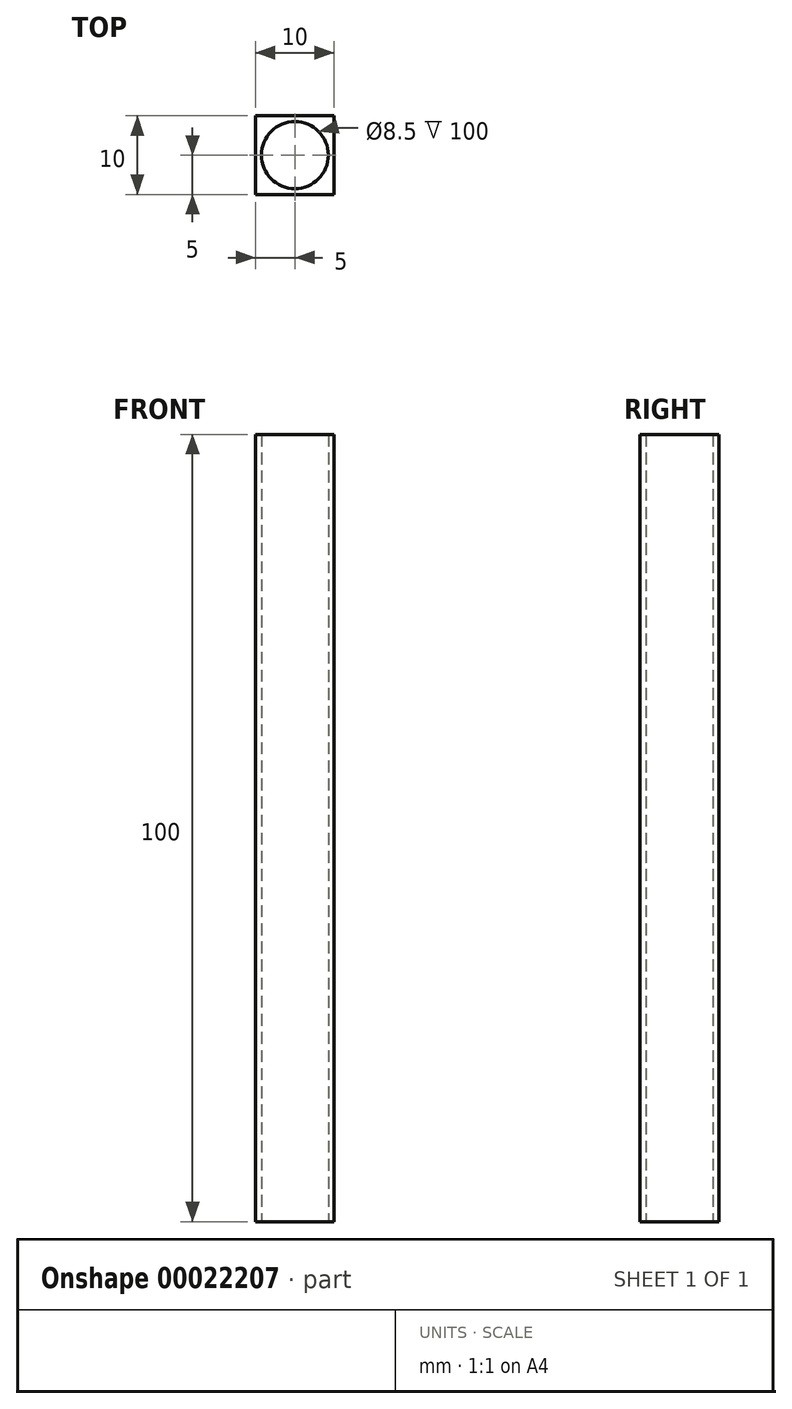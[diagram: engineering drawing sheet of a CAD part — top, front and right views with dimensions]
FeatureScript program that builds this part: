
annotation { "Feature Type Name" : "Feature", "Feature Type Description" : "" }
export const myFeature = defineFeature(function(context is Context, id is Id, definition is map)
    precondition{}
    {
        {
            var Q0;
            Q0=qCreatedBy(makeId("Top.planeOp"),FACE);
            var sketch = newSketch(context, id + "F0", { "sketchPlane" : qUnion([Q0])});
            skLineSegment(sketch, "E0.rect.bottom", {"start": v(4.5, 5) * mm, "end": v(-4.5, 5) * mm});
            skLineSegment(sketch, "E0.rect.top", {"start": v(4.5, -5) * mm, "end": v(-4.5, -5) * mm});
            skLineSegment(sketch, "E0.rect.left", {"start": v(5, 4.5) * mm, "end": v(5, -4.5) * mm});
            skLineSegment(sketch, "E0.rect.right", {"start": v(-5, 4.5) * mm, "end": v(-5, -4.5) * mm});
            skPoint(sketch, "E0.rect.middle", {"position": v(0, 0) * mm});
            skCircle(sketch, "E1", {"center": v(0, 0) * mm, "radius": 4.25 * mm});
            skPoint(sketch, "E2.visualSharp", {"position": v(-5, 5) * mm});
            skPoint(sketch, "E3.visualSharp", {"position": v(5, 5) * mm});
            skPoint(sketch, "E4.visualSharp", {"position": v(5, -5) * mm});
            skPoint(sketch, "E5.visualSharp", {"position": v(-5, -5) * mm});
            skLineSegment(sketch, "E6", {"start": v(-4.5, 5) * mm, "end": v(-5, 5) * mm});
            skLineSegment(sketch, "E7", {"start": v(-5, 4.5) * mm, "end": v(-5, 5) * mm});
            skLineSegment(sketch, "E8", {"start": v(4.5, 5) * mm, "end": v(5, 5) * mm});
            skLineSegment(sketch, "E9", {"start": v(5, 5) * mm, "end": v(5, 4.5) * mm});
            skLineSegment(sketch, "E10", {"start": v(5, -4.5) * mm, "end": v(5, -5) * mm});
            skLineSegment(sketch, "E11", {"start": v(4.5, -5) * mm, "end": v(5, -5) * mm});
            skLineSegment(sketch, "E12", {"start": v(-5, -4.5) * mm, "end": v(-5, -5) * mm});
            skLineSegment(sketch, "E13", {"start": v(-5, -5) * mm, "end": v(-4.5, -5) * mm});
            skSolve(sketch);
        }
        {
            var Q0;
            Q0=makeQuery(id+"F0.imprint","IMPRINT",FACE,{"disambiguationData":[TD([[makeQuery(id+"F0.imprint","IMPRINT",EDGE,{"derivedFrom":sQuery(id+"F0.wireOp",EDGE,"E0.rect.bottom")}),1.0]])]});
            extrude(context, id + "F1", {"entities" : qUnion([Q0]), "depth" : 100 * mm});
        }
    });
